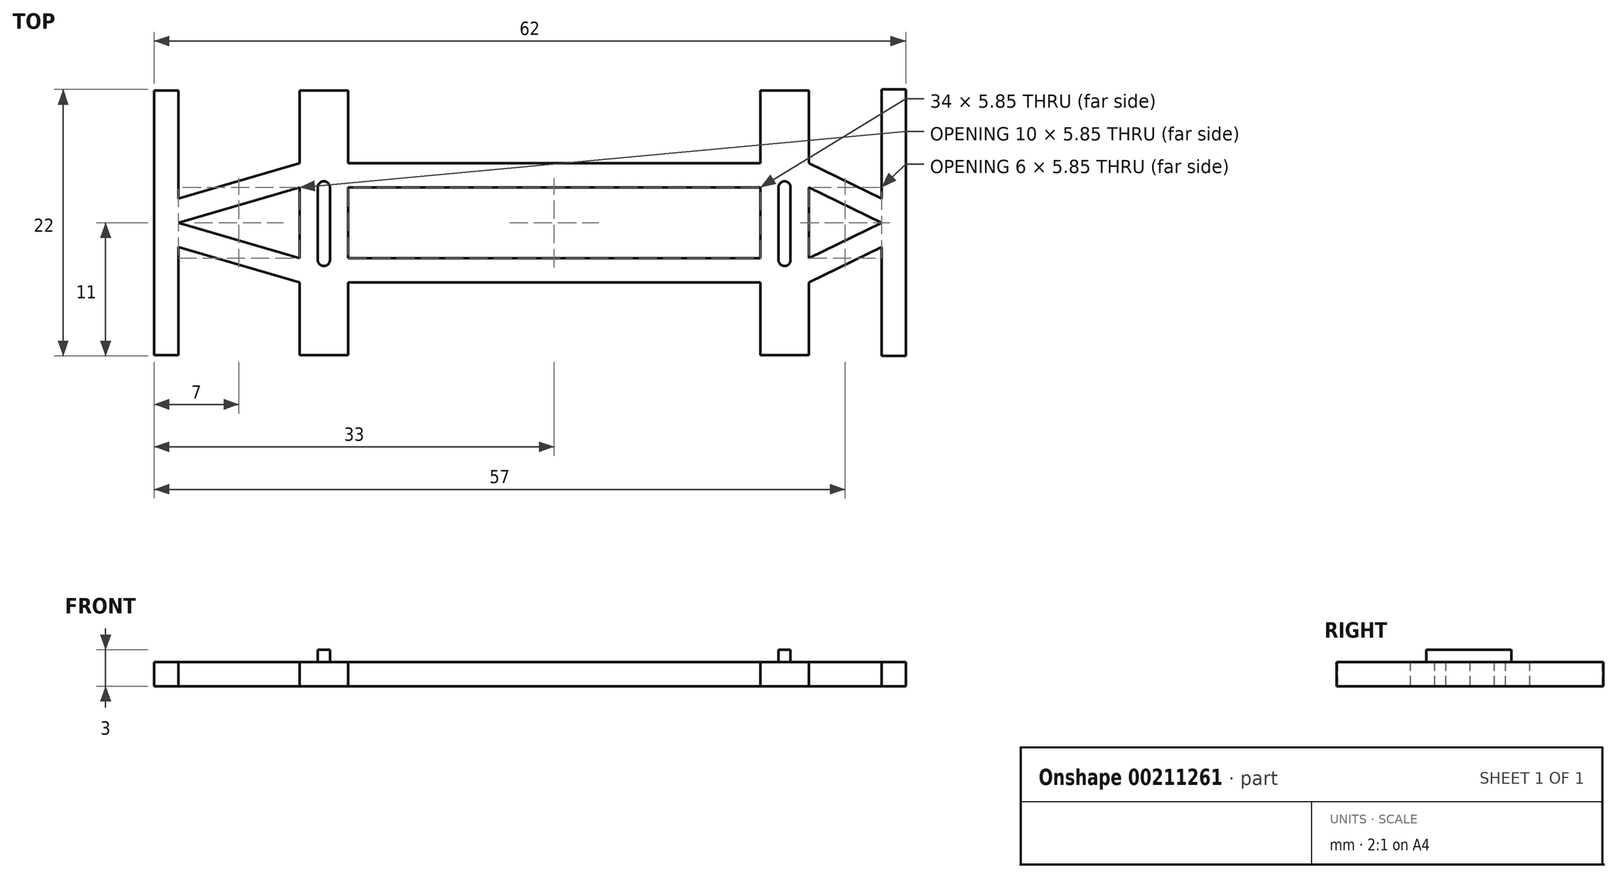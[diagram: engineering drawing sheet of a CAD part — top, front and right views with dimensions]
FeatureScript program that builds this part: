
annotation { "Feature Type Name" : "Feature", "Feature Type Description" : "" }
export const myFeature = defineFeature(function(context is Context, id is Id, definition is map)
    precondition{}
    {
        {
            var Q0;
            Q0=qCreatedBy(makeId("Top.planeOp"),FACE);
            var sketch = newSketch(context, id + "F0", { "sketchPlane" : qUnion([Q0])});
            skLineSegment(sketch, "E0", {"start": v(0, 0) * mm, "end": v(0, -11) * mm});
            skLineSegment(sketch, "E1", {"start": v(0, -11) * mm, "end": v(-2, -11) * mm});
            skLineSegment(sketch, "E2", {"start": v(-2, -11) * mm, "end": v(-2, -2) * mm});
            skLineSegment(sketch, "E3", {"start": v(-2, -2) * mm, "end": v(-8, -4.92) * mm});
            skLineSegment(sketch, "E4", {"start": v(-2, 0) * mm, "end": v(-8, -2.92) * mm});
            skLineSegment(sketch, "E5", {"start": v(-68.75, 0) * mm, "end": v(-12, 0) * mm, "construction": true});
            skLineSegment(sketch, "E6.top", {"start": v(-12, -10.92) * mm, "end": v(-8, -10.92) * mm});
            skLineSegment(sketch, "E6.left", {"start": v(-12, 0) * mm, "end": v(-12, -2.92) * mm});
            skLineSegment(sketch, "E6.right", {"start": v(-8, 0) * mm, "end": v(-8, -2.92) * mm});
            skLineSegment(sketch, "E7.trimOffspring", {"start": v(-8, -4.92) * mm, "end": v(-8, -10.92) * mm});
            skLineSegment(sketch, "E8.trimOffspring", {"start": v(-8, 0) * mm, "end": v(76.35, 0) * mm, "construction": true});
            skLineSegment(sketch, "E9", {"start": v(-12, -2.92) * mm, "end": v(-29, -2.92) * mm});
            skLineSegment(sketch, "E10", {"start": v(-12, -4.92) * mm, "end": v(-29, -4.92) * mm});
            skPoint(sketch, "E10.startSnap0", {"position": v(-12, -5.46) * mm});
            skLineSegment(sketch, "E11", {"start": v(-29, 42.65) * mm, "end": v(-29, -65.17) * mm, "construction": true});
            skLineSegment(sketch, "E12.MirrorCS", {"start": v(-12, 4.92) * mm, "end": v(-29, 4.92) * mm});
            skLineSegment(sketch, "E13.MirrorCS", {"start": v(-12, 2.92) * mm, "end": v(-29, 2.92) * mm});
            skLineSegment(sketch, "E14.MirrorCS", {"start": v(-12, 0) * mm, "end": v(-12, 2.92) * mm});
            skLineSegment(sketch, "E15.MirrorCS", {"start": v(-8, 0) * mm, "end": v(-8, 2.92) * mm});
            skLineSegment(sketch, "E16.MirrorCS", {"start": v(-8, 4.92) * mm, "end": v(-8, 10.92) * mm});
            skLineSegment(sketch, "E17.MirrorCS", {"start": v(-12, 10.92) * mm, "end": v(-8, 10.92) * mm});
            skLineSegment(sketch, "E18.MirrorCS", {"start": v(-2, 2) * mm, "end": v(-8, 4.92) * mm});
            skLineSegment(sketch, "E19.MirrorCS", {"start": v(-2, 0) * mm, "end": v(-8, 2.92) * mm});
            skLineSegment(sketch, "E20.MirrorCS", {"start": v(-2, 11) * mm, "end": v(-2, 2) * mm});
            skLineSegment(sketch, "E21.MirrorCS", {"start": v(0, 11) * mm, "end": v(-2, 11) * mm});
            skLineSegment(sketch, "E22.MirrorCS", {"start": v(0, 0) * mm, "end": v(0, 11) * mm});
            skLineSegment(sketch, "E23.trimOffspring", {"start": v(-12, 4.92) * mm, "end": v(-12, 10.92) * mm});
            skLineSegment(sketch, "E24.trimOffspring", {"start": v(-12, -4.92) * mm, "end": v(-12, -10.92) * mm});
            skLineSegment(sketch, "E25.MirrorCS", {"start": v(-46, 4.92) * mm, "end": v(-29, 4.92) * mm});
            skLineSegment(sketch, "E26.MirrorCS", {"start": v(-46, 2.92) * mm, "end": v(-29, 2.92) * mm});
            skLineSegment(sketch, "E27.MirrorCS", {"start": v(-46, -4.92) * mm, "end": v(-29, -4.92) * mm});
            skLineSegment(sketch, "E28.MirrorCS", {"start": v(-46, -2.92) * mm, "end": v(-29, -2.92) * mm});
            skLineSegment(sketch, "E29.MirrorCS", {"start": v(-46, 0) * mm, "end": v(-46, -2.92) * mm});
            skLineSegment(sketch, "E30.MirrorCS", {"start": v(-46, 0) * mm, "end": v(-46, 2.92) * mm});
            skLineSegment(sketch, "E31.MirrorCS", {"start": v(-46, 4.92) * mm, "end": v(-46, 10.92) * mm});
            skLineSegment(sketch, "E32.MirrorCS", {"start": v(-46, 10.92) * mm, "end": v(-50, 10.92) * mm});
            skLineSegment(sketch, "E33.MirrorCS", {"start": v(-50, 4.92) * mm, "end": v(-50, 10.92) * mm});
            skLineSegment(sketch, "E34.MirrorCS", {"start": v(-50, -4.92) * mm, "end": v(-50, -10.92) * mm});
            skLineSegment(sketch, "E35.MirrorCS", {"start": v(-46, -10.92) * mm, "end": v(-50, -10.92) * mm});
            skLineSegment(sketch, "E36.MirrorCS", {"start": v(-46, -4.92) * mm, "end": v(-46, -10.92) * mm});
            skPoint(sketch, "E37.MirrorCS.end.orphan", {"position": v(-50, 4.92) * mm});
            skPoint(sketch, "E38.MirrorCS.end.orphan", {"position": v(-50, -4.92) * mm});
            skLineSegment(sketch, "E39", {"start": v(-60, -2) * mm, "end": v(-60, -10.92) * mm});
            skLineSegment(sketch, "E40", {"start": v(-60, -10.92) * mm, "end": v(-62, -10.92) * mm});
            skLineSegment(sketch, "E41", {"start": v(-62, -10.92) * mm, "end": v(-62, 10.92) * mm});
            skLineSegment(sketch, "E42", {"start": v(-62, 10.92) * mm, "end": v(-60, 10.92) * mm});
            skLineSegment(sketch, "E43", {"start": v(-60, 10.92) * mm, "end": v(-60, 2) * mm});
            skLineSegment(sketch, "E44", {"start": v(-50, -4.92) * mm, "end": v(-60, -2) * mm});
            skLineSegment(sketch, "E45", {"start": v(-50, 4.92) * mm, "end": v(-60, 2) * mm});
            skPoint(sketch, "E46.startSnap0", {"position": v(-55, 3.46) * mm});
            skPoint(sketch, "E46.endSnap0", {"position": v(-55, -3.46) * mm});
            skLineSegment(sketch, "E47", {"start": v(-50, 2.92) * mm, "end": v(-60, 0) * mm});
            skLineSegment(sketch, "E48", {"start": v(-60, 0) * mm, "end": v(-50, -2.92) * mm});
            skLineSegment(sketch, "E49", {"start": v(-50, -2.92) * mm, "end": v(-50, 2.92) * mm});
            skSolve(sketch);
        }
        {
            var Q0;
            Q0=qSketchRegion(id+"F0",true);
            extrude(context, id + "F1", {"entities" : qUnion([Q0]), "depth" : 2 * mm});
        }
        {
            var Q0;
            Q0=makeQuery(id+"F1.opExtrude","CAP_FACE",FACE,{"disambiguationData":[OSD([sQuery(id+"F0.wireOp",EDGE,"E0"),sQuery(id+"F0.wireOp",EDGE,"E1"),sQuery(id+"F0.wireOp",EDGE,"E2"),sQuery(id+"F0.wireOp",EDGE,"E3"),sQuery(id+"F0.wireOp",EDGE,"E4"),sQuery(id+"F0.wireOp",EDGE,"E6.top"),sQuery(id+"F0.wireOp",EDGE,"E6.left"),sQuery(id+"F0.wireOp",EDGE,"E6.right"),sQuery(id+"F0.wireOp",EDGE,"E7.trimOffspring"),sQuery(id+"F0.wireOp",EDGE,"E9"),sQuery(id+"F0.wireOp",EDGE,"E10"),sQuery(id+"F0.wireOp",EDGE,"E12.MirrorCS"),sQuery(id+"F0.wireOp",EDGE,"E13.MirrorCS"),sQuery(id+"F0.wireOp",EDGE,"E15.MirrorCS"),sQuery(id+"F0.wireOp",EDGE,"E16.MirrorCS"),sQuery(id+"F0.wireOp",EDGE,"E14.MirrorCS"),sQuery(id+"F0.wireOp",EDGE,"E17.MirrorCS"),sQuery(id+"F0.wireOp",EDGE,"E18.MirrorCS"),sQuery(id+"F0.wireOp",EDGE,"E19.MirrorCS"),sQuery(id+"F0.wireOp",EDGE,"E20.MirrorCS"),sQuery(id+"F0.wireOp",EDGE,"E21.MirrorCS"),sQuery(id+"F0.wireOp",EDGE,"E22.MirrorCS"),sQuery(id+"F0.wireOp",EDGE,"E24.trimOffspring"),sQuery(id+"F0.wireOp",EDGE,"E23.trimOffspring"),sQuery(id+"F0.wireOp",EDGE,"E25.MirrorCS"),sQuery(id+"F0.wireOp",EDGE,"E26.MirrorCS"),sQuery(id+"F0.wireOp",EDGE,"E27.MirrorCS"),sQuery(id+"F0.wireOp",EDGE,"E28.MirrorCS"),sQuery(id+"F0.wireOp",EDGE,"E29.MirrorCS"),sQuery(id+"F0.wireOp",EDGE,"E30.MirrorCS"),sQuery(id+"F0.wireOp",EDGE,"E31.MirrorCS"),sQuery(id+"F0.wireOp",EDGE,"E32.MirrorCS"),sQuery(id+"F0.wireOp",EDGE,"E33.MirrorCS"),sQuery(id+"F0.wireOp",EDGE,"E34.MirrorCS"),sQuery(id+"F0.wireOp",EDGE,"E35.MirrorCS"),sQuery(id+"F0.wireOp",EDGE,"E36.MirrorCS"),sQuery(id+"F0.wireOp",EDGE,"E39"),sQuery(id+"F0.wireOp",EDGE,"E40"),sQuery(id+"F0.wireOp",EDGE,"E41"),sQuery(id+"F0.wireOp",EDGE,"E42"),sQuery(id+"F0.wireOp",EDGE,"E43"),sQuery(id+"F0.wireOp",EDGE,"E44"),sQuery(id+"F0.wireOp",EDGE,"E45"),sQuery(id+"F0.wireOp",EDGE,"E47"),sQuery(id+"F0.wireOp",EDGE,"E48"),sQuery(id+"F0.wireOp",EDGE,"E49")])],"isStart":false});
            var sketch = newSketch(context, id + "F2", { "sketchPlane" : qUnion([Q0])});
            skLineSegment(sketch, "E50", {"start": v(-48, 2.92) * mm, "end": v(-48, -3.08) * mm, "construction": true});
            skPoint(sketch, "E50.startSnap0", {"position": v(-48, 10.92) * mm});
            skArc(sketch, "E51", {"start": v(-47.5, 2.92) * mm, "mid": v(-48, 3.42) * mm, "end": v(-48.5, 2.92) * mm});
            skArc(sketch, "E52", {"start": v(-47.5, -3.08) * mm, "mid": v(-48, -3.58) * mm, "end": v(-48.5, -3.08) * mm});
            skLineSegment(sketch, "E53", {"start": v(-48.5, 2.92) * mm, "end": v(-48.5, -3.08) * mm});
            skLineSegment(sketch, "E54", {"start": v(-47.5, 2.92) * mm, "end": v(-47.5, -3.08) * mm});
            skLineSegment(sketch, "E55", {"start": v(-70.51, 2.92) * mm, "end": v(-48, 2.92) * mm, "construction": true});
            skLineSegment(sketch, "E56", {"start": v(-29, 29.5) * mm, "end": v(-29, -26.1) * mm, "construction": true});
            skPoint(sketch, "E56.startSnap0", {"position": v(-29, 4.92) * mm});
            skLineSegment(sketch, "E57.MirrorCS", {"start": v(-9.5, 2.92) * mm, "end": v(-9.5, -3.08) * mm});
            skLineSegment(sketch, "E58.MirrorCS", {"start": v(-10.5, 2.92) * mm, "end": v(-10.5, -3.08) * mm});
            skArc(sketch, "E59.MirrorCS", {"start": v(-10.5, -3.08) * mm, "mid": v(-10, -3.58) * mm, "end": v(-9.5, -3.08) * mm});
            skArc(sketch, "E60.MirrorCS", {"start": v(-10.5, 2.92) * mm, "mid": v(-10, 3.42) * mm, "end": v(-9.5, 2.92) * mm});
            skLineSegment(sketch, "E61.MirrorCS", {"start": v(-10, 2.92) * mm, "end": v(-10, -3.08) * mm, "construction": true});
            skSolve(sketch);
        }
        {
            var Q0;
            Q0=qSketchRegion(id+"F2",true);
            extrude(context, id + "F3", {"entities" : qUnion([Q0]), "operationType" : NewBodyOperationType.ADD, "depth" : 1 * mm});
        }
    });
